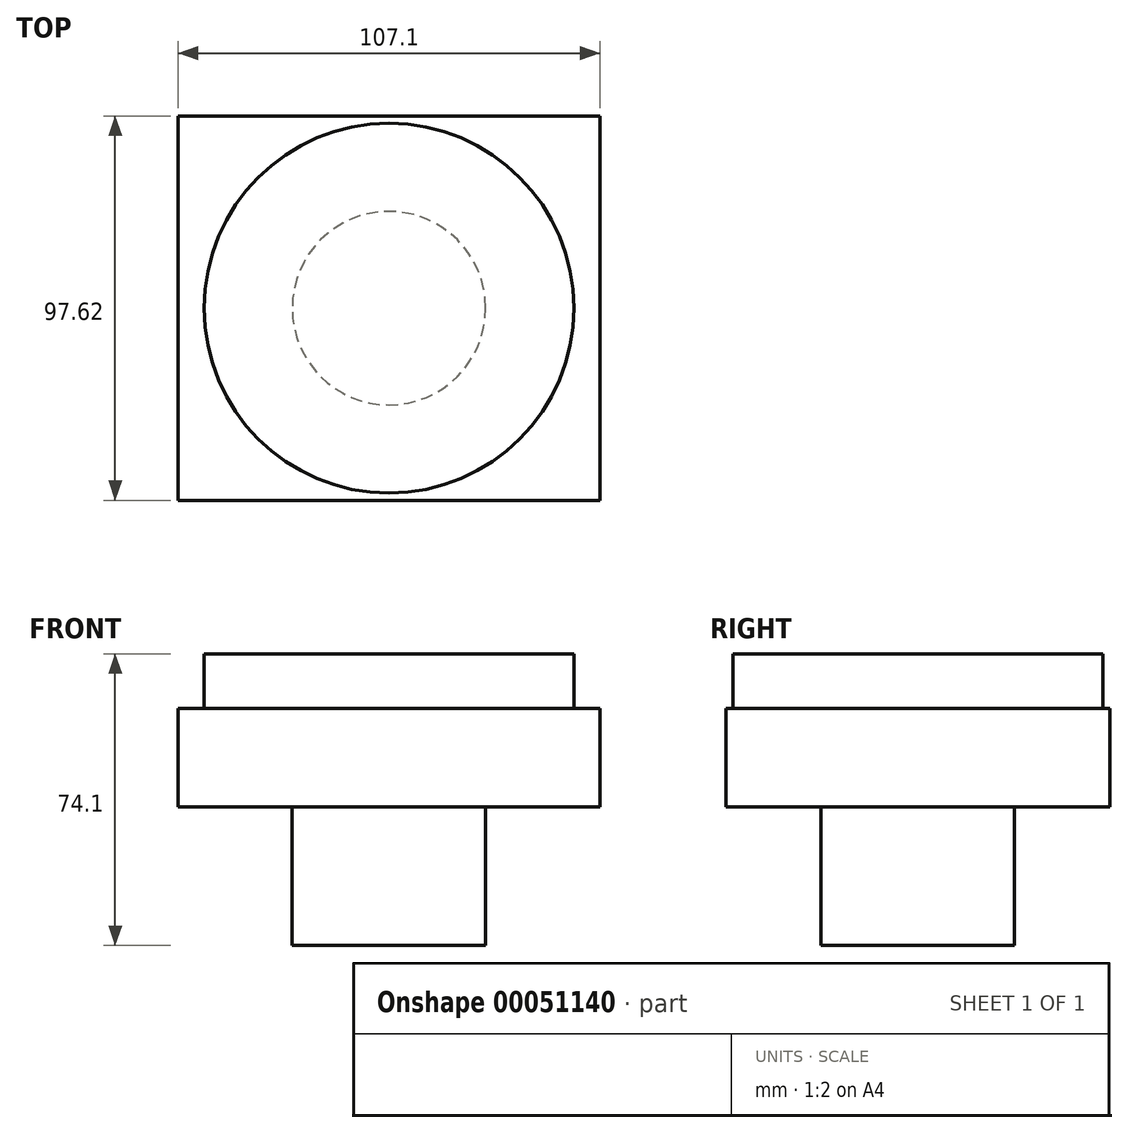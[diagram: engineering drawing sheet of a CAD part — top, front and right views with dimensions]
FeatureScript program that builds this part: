
annotation { "Feature Type Name" : "Feature", "Feature Type Description" : "" }
export const myFeature = defineFeature(function(context is Context, id is Id, definition is map)
    precondition{}
    {
        {
            var Q0;
            Q0=qCreatedBy(makeId("Top.planeOp"),FACE);
            var sketch = newSketch(context, id + "F0", { "sketchPlane" : qUnion([Q0])});
            skLineSegment(sketch, "E0.bottom", {"start": v(53.55, -48.81) * mm, "end": v(-53.55, -48.81) * mm});
            skLineSegment(sketch, "E0.top", {"start": v(53.55, 48.81) * mm, "end": v(-53.55, 48.81) * mm});
            skLineSegment(sketch, "E0.left", {"start": v(53.55, -48.81) * mm, "end": v(53.55, 48.81) * mm});
            skLineSegment(sketch, "E0.right", {"start": v(-53.55, -48.81) * mm, "end": v(-53.55, 48.81) * mm});
            skPoint(sketch, "E0.middle", {"position": v(0, 0) * mm});
            skSolve(sketch);
        }
        {
            var Q0;
            Q0 = qSketchRegion(id + "F0", true);
            extrude(context, id + "F1", {"entities" : qUnion([Q0]), "depth" : 25 * mm, "offsetDistance" : 25 * mm});
        }
        {
            var Q0;
            Q0=makeQuery(id+"F1.opExtrude","CAP_FACE",FACE,{"disambiguationData":[OSD([sQuery(id+"F0.wireOp",EDGE,"E0.bottom"),sQuery(id+"F0.wireOp",EDGE,"E0.top"),sQuery(id+"F0.wireOp",EDGE,"E0.left"),sQuery(id+"F0.wireOp",EDGE,"E0.right")])],"isStart":false});
            var sketch = newSketch(context, id + "F2", { "sketchPlane" : qUnion([Q0])});
            skCircle(sketch, "E1", {"center": v(0, 0) * mm, "radius": 24.57 * mm});
            skSolve(sketch);
        }
        {
            var Q0;
            Q0 = qSketchRegion(id + "F2", true);
            extrude(context, id + "F3", {"entities" : qUnion([Q0]), "operationType" : NewBodyOperationType.REMOVE, "endBound" : BoundingType.THROUGH_ALL, "oppositeDirection" : true, "depth" : 58.3 * mm, "offsetDistance" : 25 * mm});
        }
        {
            var Q0;
            Q0=makeQuery(id+"F1.opExtrude","CAP_FACE",FACE,{"disambiguationData":[OSD([sQuery(id+"F0.wireOp",EDGE,"E0.bottom"),sQuery(id+"F0.wireOp",EDGE,"E0.top"),sQuery(id+"F0.wireOp",EDGE,"E0.left"),sQuery(id+"F0.wireOp",EDGE,"E0.right")])],"isStart":false});
            var sketch = newSketch(context, id + "F4", { "sketchPlane" : qUnion([Q0])});
            skCircle(sketch, "E2.0", {"center": v(0, 0) * mm, "radius": 24.57 * mm});
            skSolve(sketch);
        }
        {
            var Q0;
            Q0 = qSketchRegion(id + "F4", true);
            extrude(context, id + "F5", {"entities" : qUnion([Q0]), "oppositeDirection" : true, "depth" : 60.2 * mm, "offsetDistance" : 25 * mm});
        }
        {
            var Q0;
            Q0=makeQuery(id+"F5.opExtrude","CAP_FACE",FACE,{"disambiguationData":[OSD([sQuery(id+"F4.wireOp",EDGE,"E2.0")])],"isStart":true});
            var sketch = newSketch(context, id + "F6", { "sketchPlane" : qUnion([Q0])});
            skCircle(sketch, "E3", {"center": v(0, 0) * mm, "radius": 46.97 * mm});
            skSolve(sketch);
        }
        {
            var Q0;
            Q0 = qSketchRegion(id + "F6", true);
            extrude(context, id + "F7", {"entities" : qUnion([Q0]), "operationType" : NewBodyOperationType.ADD, "depth" : 13.9 * mm, "offsetDistance" : 25 * mm});
        }
    });
